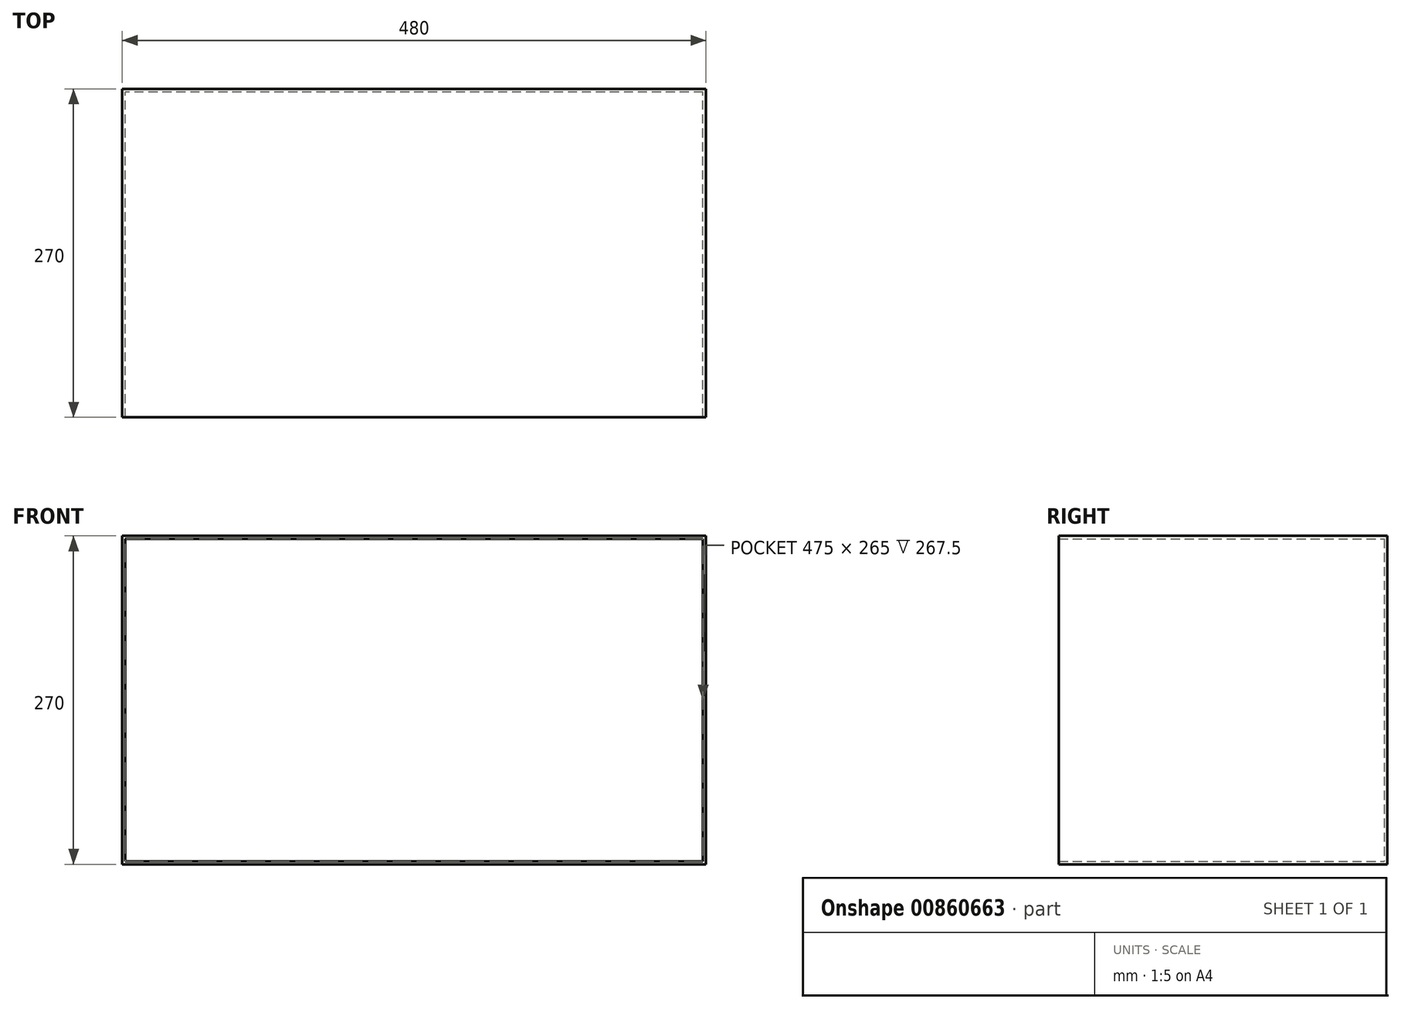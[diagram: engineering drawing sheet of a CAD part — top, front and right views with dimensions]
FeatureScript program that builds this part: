
annotation { "Feature Type Name" : "Feature", "Feature Type Description" : "" }
export const myFeature = defineFeature(function(context is Context, id is Id, definition is map)
    precondition{}
    {
        {
            var Q0;
            Q0=qCreatedBy(makeId("Top.planeOp"),FACE);
            var sketch = newSketch(context, id + "F0", { "sketchPlane" : qUnion([Q0])});
            skLineSegment(sketch, "E0.bottom", {"start": v(240, -135) * mm, "end": v(-240, -135) * mm});
            skLineSegment(sketch, "E0.top", {"start": v(240, 135) * mm, "end": v(-240, 135) * mm});
            skLineSegment(sketch, "E0.left", {"start": v(240, -135) * mm, "end": v(240, 135) * mm});
            skLineSegment(sketch, "E0.right", {"start": v(-240, -135) * mm, "end": v(-240, 135) * mm});
            skPoint(sketch, "E0.middle", {"position": v(0, 0) * mm});
            skSolve(sketch);
        }
        {
            var Q0;
            Q0=makeQuery(id+"F0.imprint","IMPRINT",FACE,{"disambiguationData":[TD([[makeQuery(id+"F0.imprint","IMPRINT",EDGE,{"derivedFrom":sQuery(id+"F0.wireOp",EDGE,"E0.bottom")}),-1.0]])]});
            extrude(context, id + "F1", {"entities" : qUnion([Q0]), "depth" : 135 * mm, "offsetDistance" : 25 * mm});
        }
        {
            var Q0;
            Q0=makeQuery(id+"F1.opExtrude","CAP_FACE",FACE,{"disambiguationData":[OSD([sQuery(id+"F0.wireOp",EDGE,"E0.bottom"),sQuery(id+"F0.wireOp",EDGE,"E0.top"),sQuery(id+"F0.wireOp",EDGE,"E0.left"),sQuery(id+"F0.wireOp",EDGE,"E0.right")])],"isStart":true});
            extrude(context, id + "F2", {"entities" : qUnion([Q0]), "operationType" : NewBodyOperationType.ADD, "depth" : 135 * mm, "offsetDistance" : 25 * mm});
        }
        {
            var Q0;
            {var subQ0=sQuery(id+"F0.wireOp",EDGE,"E0.bottom");Q0=makeQuery(id+"F2.boolean.opBoolean","MERGE",FACE,{"derivedFrom":[makeQuery(id+"F1.opExtrude","SWEPT_FACE",FACE,{"disambiguationData":[OSD([subQ0])]}),makeQuery(id+"F2.opExtrude","SWEPT_FACE",FACE,{"disambiguationData":[OSD([subQ0])]})]});}
            shell(context, id + "F3", {"entities" : qUnion([Q0]), "thickness" : 2.5 * mm});
        }
    });
